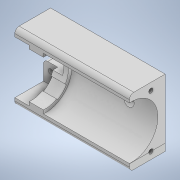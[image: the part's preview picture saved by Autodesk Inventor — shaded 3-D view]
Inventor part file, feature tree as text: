
AUTODESK INVENTOR PART (.ipt)
format: ipt  version: 2020 (Build 240168000, 168)  size: 296,448 bytes
history: native  units: in
note: dims shown in document units (in); Inventor stores cm internally (conversion verified against a paired STEP export)
features: extrude x6, sketch x6, plane x5, fillet x2, other x1
ambient origin geometry x8: Origin, YZ Plane, XZ Plane, XY Plane, X Axis, Y Axis, Z Axis, Center Point
bodies: Solid1 (feature_tree)
feature tree (20):
  extrude  "Extrusion1"  Depth=0.9843in TaperAngle=0.0deg
  extrude  "Extrusion2"  Depth=0.9213in
  plane  "Work Plane1"
  plane  "Work Plane2"
  extrude  "Extrusion3"  Depth=0.1969in
  plane  "Work Plane3"
  extrude  "Extrusion4"  Depth=0.1969in
  fillet  "Fillet1"  Radius=0.1969in
  plane  "Work Plane4"
  extrude  "Extrusion5"  TaperAngle=0.0deg  [1 undecoded]
  plane  "Work Plane5"
  extrude  "Extrusion6"  Depth=0.1181in
  fillet  "Fillet2"  [1 undecoded]
  other  "Base motor"
  sketch  "Sketch8"  dims[d13=0.3937in d14=0.0in d15=0.0in]
  sketch  "Sketch3"  dims[d5=0.0in d6=0.9213in]
  sketch  "Sketch2"  dims[d1=0.1969in d2=0.0in d3=0.9843in d4=0.0in]
  sketch  "Sketch4"  dims[d7=0.0in d9=0.1969in]
  sketch  "Sketch7"  dims[d10=0.1969in d11=0.1969in d12=0.1969in]
  sketch  "Sketch9"  dims[d16=2.7559in d17=0.0in d18=0.1181in d19=0.0in d20=0.1969in d21=0.3937in d22=0.1969in d23=0.3937in d24=0.1181in d25=0.1181in d26=0.7874in d27=0.0in d28=1.9685in d29=0.7244in d30=0.125in d31=-0.9843in d32=0.1969in d33=0.1969in d34=1.9685in d35=0.7244in d36=0.125in d37=1.5748in d38=0.0in d39=0.0787in d8=0.0344in]
note: 2 required parameter values undecoded (feature->parameter linkage not recoverable at this tier; creation-order binding heuristic only, values carry confidence <= 0.55)
